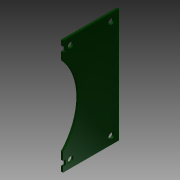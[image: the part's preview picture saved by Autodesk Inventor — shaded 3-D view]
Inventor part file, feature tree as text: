
AUTODESK INVENTOR PART (.ipt)
format: ipt  version: 2013 (Build 170138000, 138)  size: 116,736 bytes
history: native  units: in
note: dims shown in document units (in); Inventor stores cm internally (conversion verified against a paired STEP export)
features: extrude x1, sketch x1
ambient origin geometry x8: Origin, YZ Plane, XZ Plane, XY Plane, X Axis, Y Axis, Z Axis, Center Point
bodies: Solid1 (feature_tree)
feature tree (2):
  extrude  "Extrusion1"  Depth=1.1in
  sketch  "Sketch1"  dims[d0=2.25in d1=1.1in d2=1.1in d3=0.5841in d4=1.1471in d5=0.1102in d6=0.15in d7=0.15in d8=0.1in d9=0.05in d10=0.1in d11=0.05in d12=0.0394in d13=0.0in d14=0.1102in d15=0.8in d16=0.35in d17=0.35in]
